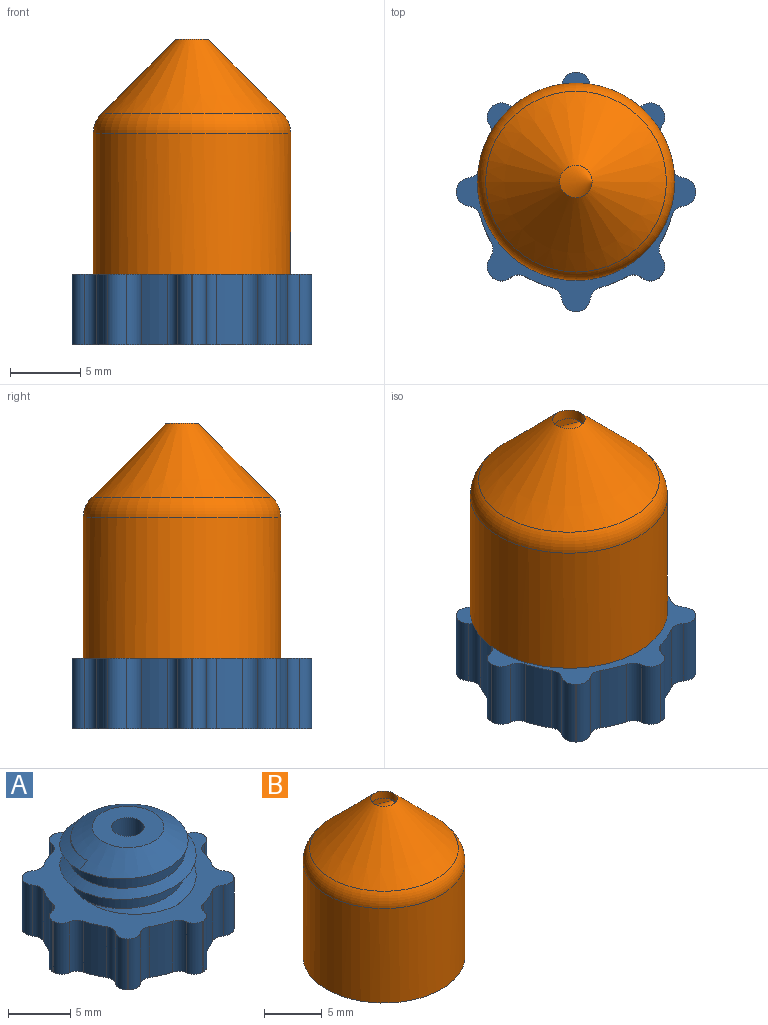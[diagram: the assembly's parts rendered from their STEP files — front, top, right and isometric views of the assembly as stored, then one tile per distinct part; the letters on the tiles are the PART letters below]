
ASSEMBLY  parts=2 mates=1
PART A: 56 faces, bbox 17.3x17.3x10.3 mm
  f0: cylinder r=4.6mm len=9.2mm, axis (0,0,-1), area 57.8mm2, adj f2,f3,f22,f23
  f1: plane 5.74x5.74mm, normal (0,0,1), area 20.5mm2, adj f20,f23
  f2: bspline ~12.62x10.93mm, area 59.3mm2, adj f0,f3,f22,f23
  f3: bspline ~12.62x10.93mm, area 59.3mm2, adj f0,f2,f22,f23
  f4: cylinder r=7mm len=5mm, axis (0,0,1), area 9.8mm2, adj f21,f22,f24,f27
  f5: plane 5x0.02mm, normal (0.71,0.71,0), area 0.2mm2, adj f21,f22,f42,f43
  f6: cylinder r=7mm len=5mm, axis (0,0,1), area 9.8mm2, adj f21,f22,f26,f29
  f7: plane 5x0.03mm, normal (0,1,0), area 0.2mm2, adj f21,f22,f44,f45
  f8: cylinder r=7mm len=5mm, axis (0,0,1), area 9.8mm2, adj f21,f22,f28,f31
  f9: plane 5x0.02mm, normal (-0.71,0.71,0), area 0.2mm2, adj f21,f22,f46,f47
  f10: cylinder r=7mm len=5mm, axis (0,0,1), area 9.8mm2, adj f21,f22,f30,f33
  f11: plane 5x0.03mm, normal (-1,0,0), area 0.2mm2, adj f21,f22,f48,f49
  f12: cylinder r=7mm len=5mm, axis (0,0,1), area 9.8mm2, adj f21,f22,f32,f35
  f13: plane 5x0.02mm, normal (-0.71,-0.71,0), area 0.2mm2, adj f21,f22,f50,f51
  f14: cylinder r=7mm len=5mm, axis (0,0,1), area 9.8mm2, adj f21,f22,f34,f37
  f15: plane 5x0.03mm, normal (0,-1,0), area 0.2mm2, adj f21,f22,f52,f53
  f16: cylinder r=7mm len=5mm, axis (0,0,1), area 9.8mm2, adj f21,f22,f36,f39
  f17: plane 5x0.02mm, normal (0.71,-0.71,0), area 0.2mm2, adj f21,f22,f54,f55
  f18: cylinder r=7mm len=5mm, axis (0,0,1), area 9.8mm2, adj f21,f22,f25,f38
  f19: plane 5x0.03mm, normal (1,0,0), area 0.2mm2, adj f21,f22,f40,f41
  f20: cylinder r=1.3mm len=10mm, axis (0,0,1), area 81.7mm2, adj f1,f21
  f21: plane 17x17mm, normal (0,0,-1), area 171.8mm2, adj f4,f5,f6,f7,f8,f9,f10,f11
  f22: plane 17.32x17.32mm, normal (0,0,1), area 104mm2, adj f0,f2,f3,f4,f5,f6,f7,f8
  f23: cone r=2.21mm half-angle=60deg, axis (0,0,-1), area 54.6mm2, adj f0,f1,f2,f3
  f24: cylinder r=1mm len=5mm, axis (0,0,1), area 6mm2, adj f4,f21,f22,f40
  f25: cylinder r=1mm len=5mm, axis (0,0,1), area 6mm2, adj f18,f21,f22,f41
  f26: cylinder r=1mm len=5mm, axis (0,0,1), area 6mm2, adj f6,f21,f22,f43
  f27: cylinder r=1mm len=5mm, axis (0,0,1), area 6mm2, adj f4,f21,f22,f42
  f28: cylinder r=1mm len=5mm, axis (0,0,1), area 6mm2, adj f8,f21,f22,f45
  f29: cylinder r=1mm len=5mm, axis (0,0,1), area 6mm2, adj f6,f21,f22,f44
  f30: cylinder r=1mm len=5mm, axis (0,0,1), area 6mm2, adj f10,f21,f22,f47
  f31: cylinder r=1mm len=5mm, axis (0,0,1), area 6mm2, adj f8,f21,f22,f46
  f32: cylinder r=1mm len=5mm, axis (0,0,1), area 6mm2, adj f12,f21,f22,f49
  f33: cylinder r=1mm len=5mm, axis (0,0,1), area 6mm2, adj f10,f21,f22,f48
  f34: cylinder r=1mm len=5mm, axis (0,0,1), area 6mm2, adj f14,f21,f22,f51
  f35: cylinder r=1mm len=5mm, axis (0,0,1), area 6mm2, adj f12,f21,f22,f50
  f36: cylinder r=1mm len=5mm, axis (0,0,1), area 6mm2, adj f16,f21,f22,f53
  f37: cylinder r=1mm len=5mm, axis (0,0,1), area 6mm2, adj f14,f21,f22,f52
  f38: cylinder r=1mm len=5mm, axis (0,0,1), area 6mm2, adj f18,f21,f22,f55
  f39: cylinder r=1mm len=5mm, axis (0,0,1), area 6mm2, adj f16,f21,f22,f54
  f40: cylinder r=1mm len=5mm, axis (0,0,1), area 7.2mm2, adj f19,f21,f22,f24
  f41: cylinder r=1mm len=5mm, axis (0,0,1), area 7.2mm2, adj f19,f21,f22,f25
  f42: cylinder r=1mm len=5mm, axis (0,0,1), area 7.2mm2, adj f5,f21,f22,f27
  f43: cylinder r=1mm len=5mm, axis (0,0,1), area 7.2mm2, adj f5,f21,f22,f26
  f44: cylinder r=1mm len=5mm, axis (0,0,1), area 7.2mm2, adj f7,f21,f22,f29
  f45: cylinder r=1mm len=5mm, axis (0,0,1), area 7.2mm2, adj f7,f21,f22,f28
  f46: cylinder r=1mm len=5mm, axis (0,0,1), area 7.2mm2, adj f9,f21,f22,f31
  f47: cylinder r=1mm len=5mm, axis (0,0,1), area 7.2mm2, adj f9,f21,f22,f30
  f48: cylinder r=1mm len=5mm, axis (0,0,1), area 7.2mm2, adj f11,f21,f22,f33
  f49: cylinder r=1mm len=5mm, axis (0,0,1), area 7.2mm2, adj f11,f21,f22,f32
  f50: cylinder r=1mm len=5mm, axis (0,0,1), area 7.2mm2, adj f13,f21,f22,f35
  f51: cylinder r=1mm len=5mm, axis (0,0,1), area 7.2mm2, adj f13,f21,f22,f34
  f52: cylinder r=1mm len=5mm, axis (0,0,1), area 7.2mm2, adj f15,f21,f22,f37
  f53: cylinder r=1mm len=5mm, axis (0,0,1), area 7.2mm2, adj f15,f21,f22,f36
  f54: cylinder r=1mm len=5mm, axis (0,0,1), area 7.2mm2, adj f17,f21,f22,f39
  f55: cylinder r=1mm len=5mm, axis (0,0,1), area 7.2mm2, adj f17,f21,f22,f38
PART B: 13 faces, bbox 15.5x15.5x17.7 mm
  f0: cylinder r=5mm len=10mm, axis (0,0,-1), area 188.5mm2, adj f1,f7,f9,f10
  f1: cylinder r=5mm len=10mm, axis (0,0,-1), area 31.4mm2, adj f0,f2,f8,f9
  f2: cylinder r=5mm len=10mm, axis (0,0,-1), area 23.6mm2, adj f1,f3,f8,f9
  f3: plane 14.32x14.32mm, normal (0,0,-1), area 68.2mm2, adj f2,f4,f8,f9
  f4: cylinder r=7mm len=14mm, axis (0,0,-1), area 439.8mm2, adj f3,f12
  f5: cone r=1.15mm half-angle=45deg, axis (0,0,-1), area 176.9mm2, adj f6,f12
  f6: cylinder r=1.15mm len=2.3mm, axis (0,0,-1), area 5.5mm2, adj f5,f11
  f7: cone r=5mm half-angle=45deg, axis (0,0,-1), area 80.7mm2, adj f0,f11
  f8: bspline ~13.55x11.73mm, area 72.7mm2, adj f1,f2,f3,f9,f10
  f9: bspline ~13.55x11.73mm, area 81.1mm2, adj f0,f1,f2,f3,f8,f10
  f10: plane 1x0.87mm, normal (0,1,0), area 0.4mm2, adj f0,f8,f9
  f11: torus R=6.15mm, axis (0,0,1), area 40.7mm2, adj f6,f7
  f12: torus R=5mm, axis (0,0,1), area 67.1mm2, adj f4,f5
PLACE A t=(31.62,0.42,0)mm
PLACE B t=(-1.67,1.13,0)mm
MATE fastened B.f3 <-> A.f22  axis (0,0,-1) through (-1.67,0.68,0)mm
